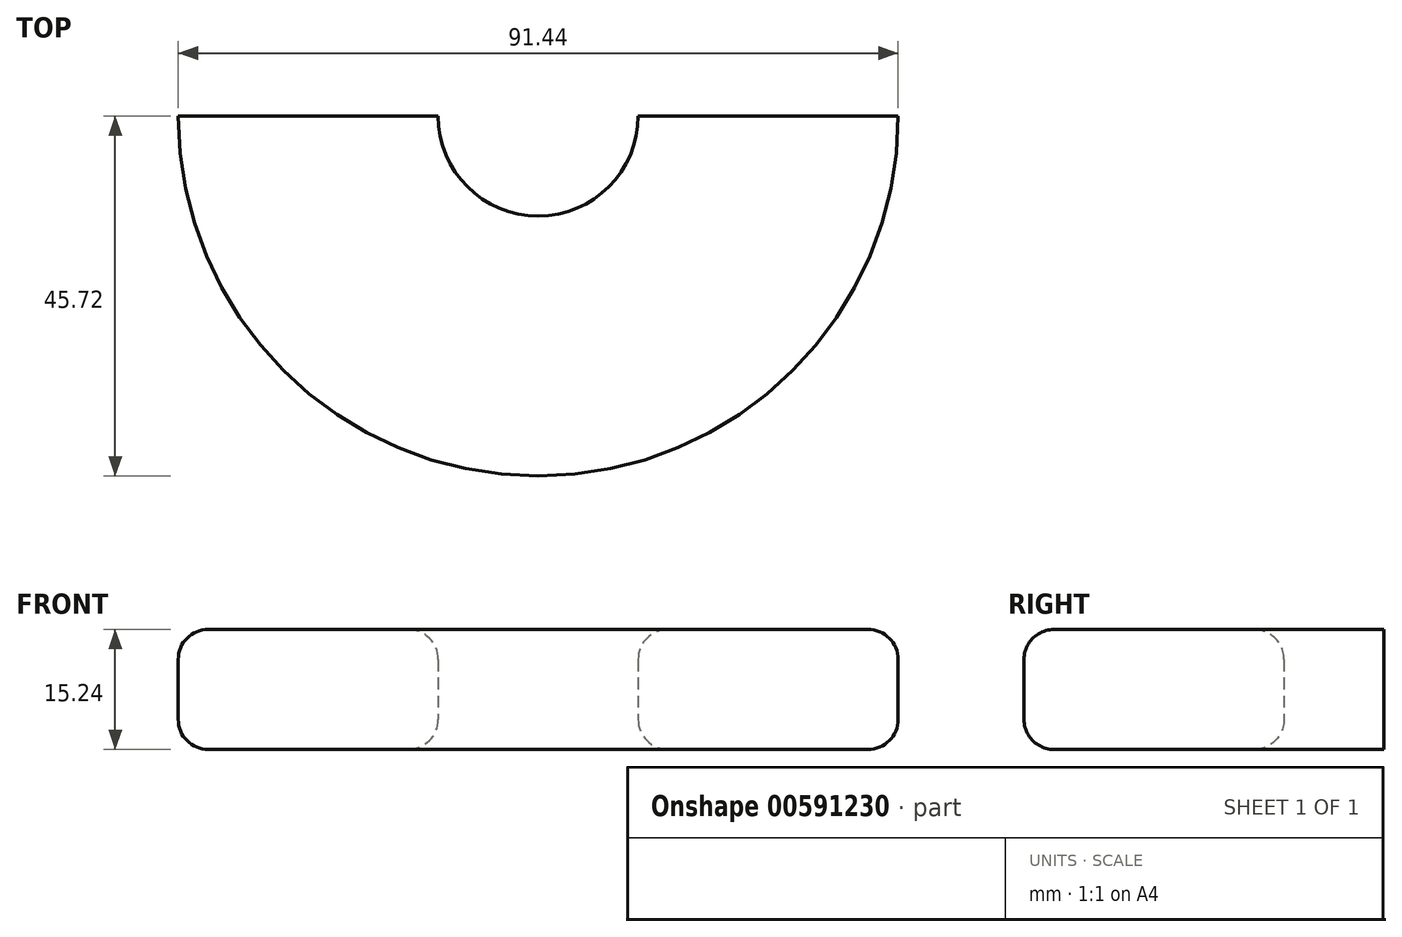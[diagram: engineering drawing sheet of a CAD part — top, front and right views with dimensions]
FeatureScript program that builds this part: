
annotation { "Feature Type Name" : "Feature", "Feature Type Description" : "" }
export const myFeature = defineFeature(function(context is Context, id is Id, definition is map)
    precondition{}
    {
        {
            var Q0;
            Q0=qCreatedBy(makeId("Front.planeOp"),FACE);
            var sketch = newSketch(context, id + "F0", { "sketchPlane" : qUnion([Q0])});
            skLineSegment(sketch, "E0", {"start": v(0, -38.1) * mm, "end": v(0, 38.1) * mm});
            skPoint(sketch, "E1", {"position": v(0, 0) * mm});
            skLineSegment(sketch, "E2.bottom", {"start": v(-41.91, 7.62) * mm, "end": v(-16.51, 7.62) * mm});
            skLineSegment(sketch, "E2.top", {"start": v(-41.91, -7.62) * mm, "end": v(-16.51, -7.62) * mm});
            skLineSegment(sketch, "E2.left", {"start": v(-45.72, 3.8) * mm, "end": v(-45.72, -3.81) * mm});
            skLineSegment(sketch, "E2.right", {"start": v(-12.7, 3.81) * mm, "end": v(-12.7, -3.81) * mm});
            skPoint(sketch, "E3.visualSharp", {"position": v(-45.72, 7.62) * mm});
            skArc(sketch, "E3.filletArc", {"start": v(-41.91, 7.62) * mm, "mid": v(-44.6, 6.5) * mm, "end": v(-45.72, 3.81) * mm});
            skPoint(sketch, "E4.visualSharp", {"position": v(-45.72, -7.62) * mm});
            skArc(sketch, "E4.filletArc", {"start": v(-45.72, -3.81) * mm, "mid": v(-44.6, -6.5) * mm, "end": v(-41.91, -7.62) * mm});
            skPoint(sketch, "E5.visualSharp", {"position": v(-12.7, -7.62) * mm});
            skArc(sketch, "E5.filletArc", {"start": v(-16.51, -7.62) * mm, "mid": v(-13.82, -6.5) * mm, "end": v(-12.7, -3.81) * mm});
            skPoint(sketch, "E6.visualSharp", {"position": v(-12.7, 7.62) * mm});
            skArc(sketch, "E6.filletArc", {"start": v(-12.7, 3.81) * mm, "mid": v(-13.82, 6.5) * mm, "end": v(-16.51, 7.62) * mm});
            skPoint(sketch, "E7", {"position": v(-12.7, 0) * mm});
            skSolve(sketch);
        }
        {
            var Q0;
            Q0 = qSketchRegion(id + "F0", true);
            var Q1;
            Q1=sQuery(id+"F0.wireOp",EDGE,"E0");
            revolve(context, id + "F1", {"surfaceOperationType" : NewSurfaceOperationType.NEW, "entities" : qUnion([Q0]), "axis" : qUnion([Q1]), "revolveType" : RevolveType.ONE_DIRECTION, "angle" : 180 * degree});
        }
    });
